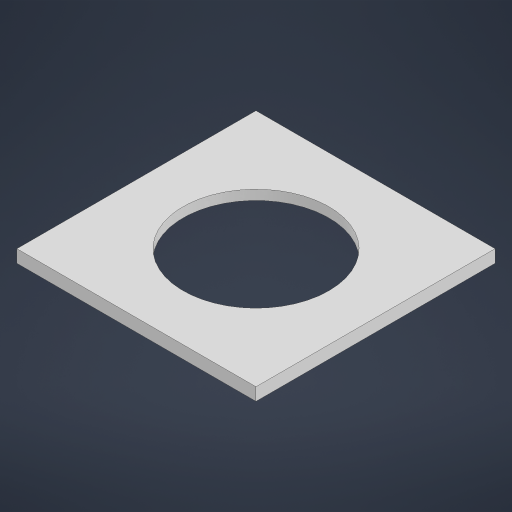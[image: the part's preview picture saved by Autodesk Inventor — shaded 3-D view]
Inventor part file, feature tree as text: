
AUTODESK INVENTOR PART (.ipt)
format: ipt  version: 2024.1 (Build 281209000, 209)  size: 183,808 bytes
history: native  units: mm
features: extrude x2, sketch x2, projected_geometry x1
ambient origin geometry x8: Origin, YZ Plane, XZ Plane, XY Plane, X Axis, Y Axis, Z Axis, Center Point
bodies: Solid1 (feature_tree)
feature tree (5):
  extrude  "Extrusion1"  Depth=18.6mm
  extrude  "Extrusion2"  Depth=0.3mm TaperAngle=0.0deg
  sketch  "Sketch1"  dims[d0=18.6mm d1=18.6mm]
  sketch  "Sketch2"  dims[d2=3.0mm d3=0.3mm d4=0.0mm d5=15.0mm d6=1.0mm d7=0.0mm]
  projected_geometry  "Projected Loop1"
